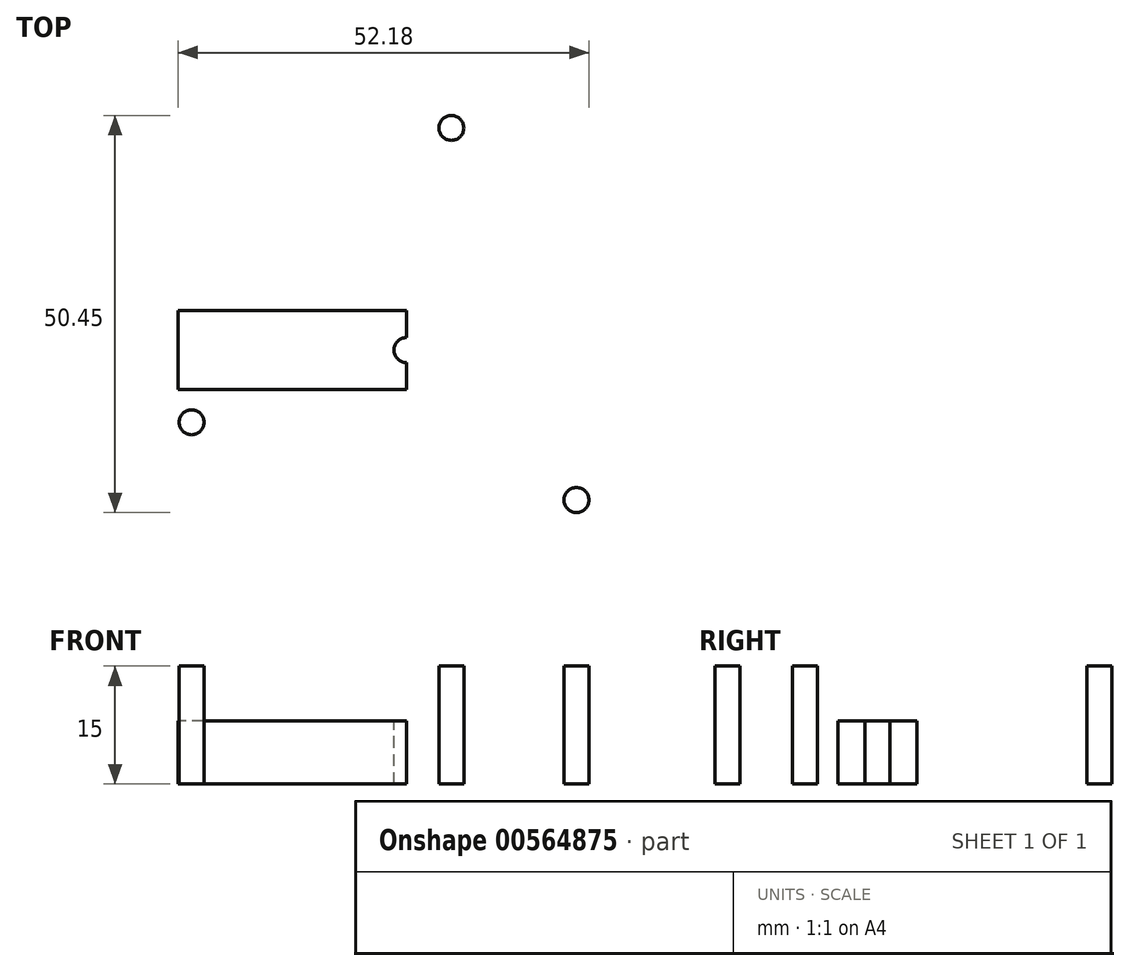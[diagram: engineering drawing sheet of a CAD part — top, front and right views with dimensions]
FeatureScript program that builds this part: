
annotation { "Feature Type Name" : "Feature", "Feature Type Description" : "" }
export const myFeature = defineFeature(function(context is Context, id is Id, definition is map)
    precondition{}
    {
        {
            var Q0;
            Q0=qCreatedBy(makeId("Top.planeOp"),FACE);
            var sketch = newSketch(context, id + "F0", { "sketchPlane" : qUnion([Q0])});
            skCircle(sketch, "E0", {"center": v(0, 0) * mm, "radius": 32.5 * mm});
            skSolve(sketch);
        }
        {
            var Q0;
            Q0 = qSketchRegion(id + "F0", true);
            extrude(context, id + "F1", {"entities" : qUnion([Q0]), "depth" : 15 * mm, "offsetDistance" : 25.4 * mm});
        }
        {
            var Q0;
            Q0=makeQuery(id+"F1.opExtrude","CAP_FACE",FACE,{"disambiguationData":[OSD([sQuery(id+"F0.wireOp",EDGE,"E0")])],"isStart":false});
            var sketch = newSketch(context, id + "F2", { "sketchPlane" : qUnion([Q0])});
            skLineSegment(sketch, "E1.bottom", {"start": v(0, 5) * mm, "end": v(-29, 5) * mm});
            skLineSegment(sketch, "E1.top", {"start": v(0, -5) * mm, "end": v(-29, -5) * mm});
            skLineSegment(sketch, "E1.left", {"start": v(0, 5) * mm, "end": v(0, -5) * mm});
            skLineSegment(sketch, "E1.right", {"start": v(-29, 5) * mm, "end": v(-29, -5) * mm});
            skSolve(sketch);
        }
        {
            var Q0;
            Q0=makeQuery(id+"F2.imprint","IMPRINT",FACE,{"disambiguationData":[TD([[makeQuery(id+"F2.imprint","IMPRINT",EDGE,{"derivedFrom":sQuery(id+"F2.wireOp",EDGE,"E1.bottom")}),1.0]])]});
            extrude(context, id + "F3", {"entities" : qUnion([Q0]), "operationType" : NewBodyOperationType.REMOVE, "oppositeDirection" : true, "depth" : 7 * mm, "offsetDistance" : 25.4 * mm});
        }
        {
            var Q0;
            {var subQ0=sQuery(id+"F2.wireOp",EDGE,"E1.right");var subQ1=sQuery(id+"F2.wireOp",EDGE,"E1.left");var subQ2=sQuery(id+"F2.wireOp",EDGE,"E1.top");var subQ3=sQuery(id+"F2.wireOp",EDGE,"E1.bottom");Q0=makeQuery(id+"FLmcAIJaPcvBYhU_1.2.F3.boolean.opBoolean","MERGE",FACE,{"derivedFrom":[makeQuery(id+"FLmcAIJaPcvBYhU_1.1.F3.boolean.opBoolean","MERGE",FACE,{"derivedFrom":[makeQuery(id+"F3.boolean.opBoolean","COPY",FACE,{"derivedFrom":makeQuery(id+"F3.opExtrude","CAP_FACE",FACE,{"disambiguationData":[OSD([subQ3,subQ2,subQ1,subQ0])],"isStart":false})}),makeQuery(id+"FLmcAIJaPcvBYhU_1.1.F3.opExtrude","CAP_FACE",FACE,{"disambiguationData":[OSD([subQ3,subQ2,subQ1,subQ0])],"isStart":false})]}),makeQuery(id+"FLmcAIJaPcvBYhU_1.2.F3.opExtrude","CAP_FACE",FACE,{"disambiguationData":[OSD([subQ3,subQ2,subQ1,subQ0])],"isStart":false})]});}
            var sketch = newSketch(context, id + "F4", { "sketchPlane" : qUnion([Q0])});
            skCircle(sketch, "E2", {"center": v(0, 0) * mm, "radius": 1.59 * mm});
            skSolve(sketch);
        }
        {
            var Q0;
            Q0=makeQuery(id+"F4.imprint","IMPRINT",FACE,{"disambiguationData":[TD([[makeQuery(id+"F4.imprint","IMPRINT",EDGE,{"derivedFrom":sQuery(id+"F4.wireOp",EDGE,"E2")}),1.0]])]});
            extrude(context, id + "F5", {"entities" : qUnion([Q0]), "operationType" : NewBodyOperationType.REMOVE, "oppositeDirection" : true, "depth" : 25.4 * mm, "offsetDistance" : 25.4 * mm});
        }
        {
            var Q0;
            Q0=makeQuery(id+"F1.opExtrude","CAP_FACE",FACE,{"disambiguationData":[OSD([sQuery(id+"F0.wireOp",EDGE,"E0")])],"isStart":false});
            var sketch = newSketch(context, id + "F6", { "sketchPlane" : qUnion([Q0])});
            skCircle(sketch, "E3", {"center": v(10.16, 0) * mm, "radius": 1.59 * mm});
            skCircle(sketch, "E4", {"center": v(21.59, 19.05) * mm, "radius": 1.59 * mm});
            skCircle(sketch, "E5.MirrorC", {"center": v(21.59, -19.05) * mm, "radius": 1.59 * mm});
            skCircle(sketch, "E6.1.0", {"center": v(-27.3, 9.17) * mm, "radius": 1.59 * mm});
            skCircle(sketch, "E6.1.1", {"center": v(5.7, 28.22) * mm, "radius": 1.59 * mm});
            skCircle(sketch, "E6.1.2", {"center": v(-5.08, 8.8) * mm, "radius": 1.59 * mm});
            skCircle(sketch, "E6.2.0", {"center": v(5.7, -28.22) * mm, "radius": 1.59 * mm});
            skCircle(sketch, "E6.2.1", {"center": v(-27.3, -9.17) * mm, "radius": 1.59 * mm});
            skCircle(sketch, "E6.2.2", {"center": v(-5.08, -8.8) * mm, "radius": 1.59 * mm});
            skPoint(sketch, "E6.center", {"position": v(0, 0) * mm});
            skSolve(sketch);
        }
        {
            var Q0;
            Q0=makeQuery(id+"F6.imprint","IMPRINT",FACE,{"disambiguationData":[TD([[makeQuery(id+"F6.imprint","IMPRINT",EDGE,{"derivedFrom":sQuery(id+"F6.wireOp",EDGE,"E3")}),1.0]])]});
            var Q1;
            Q1=makeQuery(id+"F6.imprint","IMPRINT",FACE,{"disambiguationData":[TD([[makeQuery(id+"F6.imprint","IMPRINT",EDGE,{"derivedFrom":sQuery(id+"F6.wireOp",EDGE,"E4")}),1.0]])]});
            var Q2;
            Q2=makeQuery(id+"F6.imprint","IMPRINT",FACE,{"disambiguationData":[TD([[makeQuery(id+"F6.imprint","IMPRINT",EDGE,{"derivedFrom":sQuery(id+"F6.wireOp",EDGE,"E5.MirrorC")}),-1.0]])]});
            var Q3;
            Q3=makeQuery(id+"F6.imprint","IMPRINT",FACE,{"disambiguationData":[TD([[makeQuery(id+"F6.imprint","IMPRINT",EDGE,{"derivedFrom":sQuery(id+"F6.wireOp",EDGE,"E6.1.2")}),1.0]])]});
            var Q4;
            Q4=makeQuery(id+"F6.imprint","IMPRINT",FACE,{"disambiguationData":[TD([[makeQuery(id+"F6.imprint","IMPRINT",EDGE,{"derivedFrom":sQuery(id+"F6.wireOp",EDGE,"E6.1.1")}),-1.0]])]});
            var Q5;
            Q5=makeQuery(id+"F6.imprint","IMPRINT",FACE,{"disambiguationData":[TD([[makeQuery(id+"F6.imprint","IMPRINT",EDGE,{"derivedFrom":sQuery(id+"F6.wireOp",EDGE,"E6.1.0")}),1.0]])]});
            var Q6;
            Q6=makeQuery(id+"F6.imprint","IMPRINT",FACE,{"disambiguationData":[TD([[makeQuery(id+"F6.imprint","IMPRINT",EDGE,{"derivedFrom":sQuery(id+"F6.wireOp",EDGE,"E6.2.1")}),-1.0]])]});
            var Q7;
            Q7=makeQuery(id+"F6.imprint","IMPRINT",FACE,{"disambiguationData":[TD([[makeQuery(id+"F6.imprint","IMPRINT",EDGE,{"derivedFrom":sQuery(id+"F6.wireOp",EDGE,"E6.2.2")}),1.0]])]});
            var Q8;
            Q8=makeQuery(id+"F6.imprint","IMPRINT",FACE,{"disambiguationData":[TD([[makeQuery(id+"F6.imprint","IMPRINT",EDGE,{"derivedFrom":sQuery(id+"F6.wireOp",EDGE,"E6.2.0")}),1.0]])]});
            extrude(context, id + "F7", {"entities" : qUnion([Q0, Q1, Q2, Q3, Q4, Q5, Q6, Q7, Q8]), "operationType" : NewBodyOperationType.REMOVE, "oppositeDirection" : true, "depth" : 25.4 * mm, "offsetDistance" : 25.4 * mm});
        }
    });
